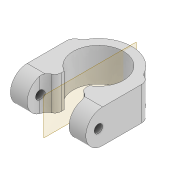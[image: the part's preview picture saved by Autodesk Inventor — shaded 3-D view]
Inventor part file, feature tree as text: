
AUTODESK INVENTOR PART (.ipt)
format: ipt  version: 2022 (Build 260153000, 153)  size: 207,360 bytes
history: native  units: mm
features: fillet x4, extrude x3, sketch x3, projected_geometry x3, thicken_offset x2, mirror x1
ambient origin geometry x8: Origin, YZ Plane, XZ Plane, XY Plane, X Axis, Y Axis, Z Axis, Center Point
bodies: Solid1 (feature_tree)
feature tree (16):
  extrude  "Extrusion1"  Depth=2.0mm
  fillet  "Fillet1"  Radius=4.0mm
  extrude  "Extrusion2"  Depth=3.0mm
  extrude  "Extrusion3"  Depth=1.5mm
  fillet  "Fillet2"  Radius=2.0mm
  mirror  "Mirror1"
  fillet  "Fillet7"  Radius=2.0mm
  thicken_offset  "Thicken1"
  thicken_offset  "Thicken2"
  fillet  "Fillet8"  Radius=100.0mm
  sketch  "Sketch1"  dims[d0=12.0mm d1=2.0mm d3=4.0mm]
  sketch  "Sketch2"  dims[d4=3.0mm d5=3.0mm]
  projected_geometry  "Projected Loop1"
  sketch  "Sketch4"  dims[d6=8.0mm d7=0.0mm d8=1.5mm d9=2.0mm d10=2.0mm d12=100.0mm d13=0.0mm d14=2.0mm d15=0.0mm d16=2.0mm d22=3.0mm d28=4.0mm d47=4.0mm d48=1.0mm d49=1.0mm d50=1.0mm d51=1.0mm d52=2.0mm d29=0.872665mm d30=0.5mm d31=0.872665mm d32=0.0mm]
  projected_geometry  "Projected Loop2"
  projected_geometry  "Projected Loop4"
